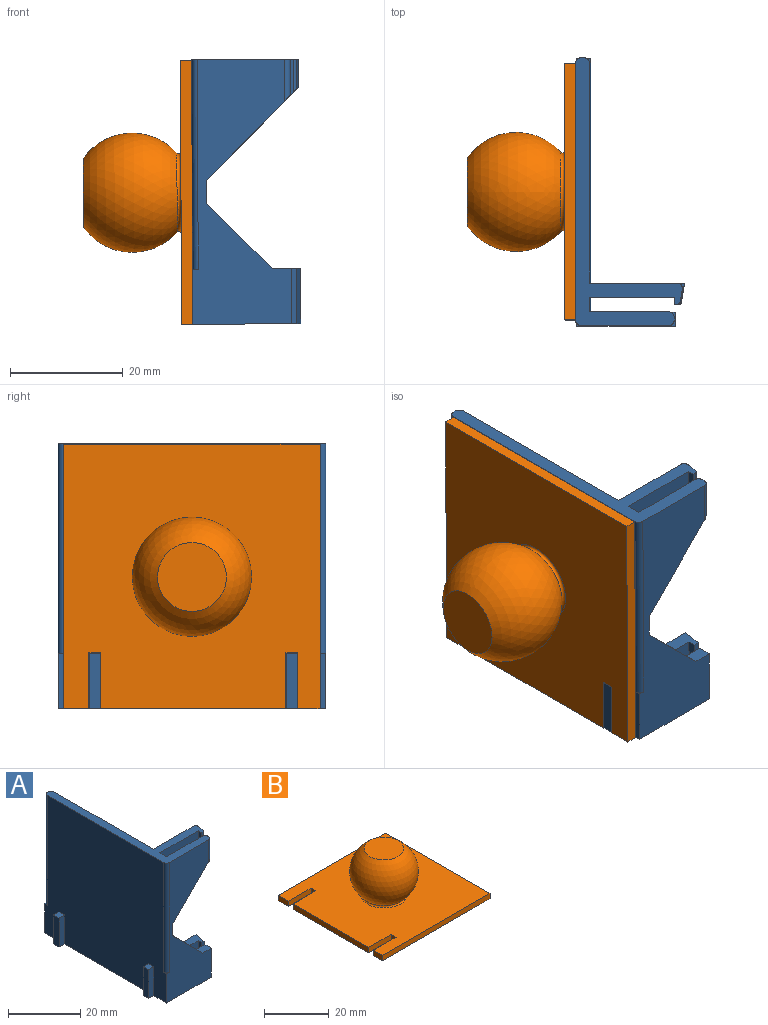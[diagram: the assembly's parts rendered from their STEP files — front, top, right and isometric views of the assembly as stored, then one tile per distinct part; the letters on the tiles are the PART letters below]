
ASSEMBLY  parts=2 mates=1
PART A: 44 faces, bbox 21.2x47.6x47 mm
  f0: plane 21.46x16.67mm, normal (0,1,0), area 231.3mm2, adj f5,f14,f19,f27,f32
  f1: plane 21.46x15mm, normal (0,1,0), area 215mm2, adj f7,f14,f19,f29,f31
  f2: plane 21.46x15mm, normal (0,-1,0), area 215mm2, adj f3,f14,f19,f27,f32
  f3: plane 9.8x1.3mm, normal (-1,0,0), area 12.7mm2, adj f2,f4,f19,f32
  f4: plane 9.8x1mm, normal (0,-1,0), area 9.8mm2, adj f3,f5,f19,f32
  f5: plane 9.8x3.79mm, normal (0.98,-0.17,0), area 37.7mm2, adj f0,f4,f19,f32
  f6: plane 47x17.49mm, normal (0,-1,0), area 497.3mm2, adj f7,f14,f16,f18,f19,f20,f24,f29
  f7: plane 9.8x2.49mm, normal (1,0,0), area 24.4mm2, adj f1,f6,f19,f31
  f8: plane 21.46x14mm, normal (0,1,0), area 202.5mm2, adj f14,f18,f21,f30
  f9: plane 21.46x15mm, normal (0,-1,0), area 209.4mm2, adj f10,f14,f18,f28
  f10: plane 6.46x1.3mm, normal (-1,0,0), area 8.4mm2, adj f9,f11,f18,f28
  f11: plane 6.46x0.58mm, normal (0,-1,0), area 3.6mm2, adj f10,f18,f26,f28
  f12: plane 5.39x2.2mm, normal (0.98,-0.17,0), area 11.6mm2, adj f18,f25,f26,f28
  f13: plane 21.46x15.48mm, normal (0,1,0), area 212.4mm2, adj f14,f18,f25,f28
  f14: plane 47.58x47mm, normal (1,0,0), area 1985.3mm2, adj f0,f1,f2,f6,f8,f9,f13,f15
  f15: plane 47x2.49mm, normal (0,1,0), area 42.6mm2, adj f14,f16,f18,f19,f22,f23,f34,f35
  f16: plane 47.58x47mm, normal (-1,0,0), area 2122.7mm2, adj f6,f15,f18,f19,f23,f24,f33,f34
  f17: plane 6.46x0.49mm, normal (1,0,0), area 3.2mm2, adj f18,f20,f21,f30
  f18: plane 47.58x18.97mm, normal (0,0,1), area 196.8mm2, adj f6,f8,f9,f10,f11,f12,f13,f14
  f19: plane 47.58x21.16mm, normal (0,0,-1), area 206.2mm2, adj f0,f1,f2,f3,f4,f5,f6,f7
  f20: cylinder r=1mm len=7.46mm, axis (0,0,-1), area 10.7mm2, adj f6,f17,f18,f30
  f21: cylinder r=1mm len=7.46mm, axis (0,0,-1), area 10.7mm2, adj f8,f17,f18,f30
  f22: cylinder r=1mm len=37.2mm, axis (0,0,1), area 58.4mm2, adj f14,f15,f18,f35
  f23: cylinder r=1mm len=37.2mm, axis (0,0,-1), area 58.4mm2, adj f15,f16,f18,f34
  f24: cylinder r=1mm len=37.2mm, axis (0,0,1), area 58.4mm2, adj f6,f16,f18,f33
  f25: cylinder r=1mm len=5.99mm, axis (0,0,1), area 9.3mm2, adj f12,f13,f18,f28
  f26: cylinder r=0.5mm len=5.88mm, axis (0,0,-1), area 3.9mm2, adj f11,f12,f18,f28
  f27: plane 11.66x11.66mm, normal (0.71,0,0.71), area 41.1mm2, adj f0,f2,f14,f32
  f28: plane 16.48x16.48mm, normal (0.71,0,-0.71), area 59.5mm2, adj f9,f10,f11,f12,f13,f14,f25,f26
  f29: plane 11.66x11.66mm, normal (0.71,0,0.71), area 41.1mm2, adj f1,f6,f14,f31
  f30: plane 15x15mm, normal (0.71,0,-0.71), area 52.2mm2, adj f6,f8,f14,f17,f20,f21
  f31: plane 3.34x2.49mm, normal (0,0,1), area 8.3mm2, adj f1,f6,f7,f29
  f32: plane 5.01x3.79mm, normal (0,0,1), area 13.4mm2, adj f0,f2,f3,f4,f5,f27
  f33: plane 1x1mm, normal (0,0,1), area 0.2mm2, adj f6,f16,f24
  f34: plane 1x1mm, normal (0,0,1), area 0.2mm2, adj f15,f16,f23
  f35: plane 1x1mm, normal (0,0,1), area 0.2mm2, adj f14,f15,f22
  f36: plane 9.8x2mm, normal (-1,0,0), area 19.6mm2, adj f19,f37,f38,f39
  f37: plane 2x2mm, normal (0,0,1), area 4mm2, adj f16,f36,f38,f39
  f38: plane 9.8x2mm, normal (0,1,0), area 19.6mm2, adj f16,f19,f36,f37
  f39: plane 9.8x2mm, normal (0,-1,0), area 19.6mm2, adj f16,f19,f36,f37
  f40: plane 2x2mm, normal (0,0,1), area 4mm2, adj f16,f41,f42,f43
  f41: plane 9.8x2mm, normal (0,1,0), area 19.6mm2, adj f16,f19,f40,f42
  f42: plane 9.8x2mm, normal (-1,0,0), area 19.6mm2, adj f19,f40,f41,f43
  f43: plane 9.8x2mm, normal (0,-1,0), area 19.6mm2, adj f16,f19,f40,f42
PART B: 17 faces, bbox 47x45.5x19.3 mm
  f0: sphere r=10.6mm, area 1106.9mm2, adj f15,f16
  f1: plane 45.5x2mm, normal (1,0,0), area 91mm2, adj f2,f12,f13,f14
  f2: plane 47x2mm, normal (0,-1,0), area 94mm2, adj f1,f3,f13,f14
  f3: plane 3.95x2mm, normal (-1,0,0), area 7.9mm2, adj f2,f4,f13,f14
  f4: plane 10x2mm, normal (0,1,0), area 20mm2, adj f3,f5,f13,f14
  f5: plane 2.1x2mm, normal (-1,0,0), area 4.2mm2, adj f4,f6,f13,f14
  f6: plane 10x2mm, normal (0,-1,0), area 20mm2, adj f5,f7,f13,f14
  f7: plane 32.9x2mm, normal (-1,0,0), area 65.8mm2, adj f6,f8,f13,f14
  f8: plane 10x2mm, normal (0,1,0), area 20mm2, adj f7,f9,f13,f14
  f9: plane 2.1x2mm, normal (-1,0,0), area 4.2mm2, adj f8,f10,f13,f14
  f10: plane 10x2mm, normal (0,-1,0), area 20mm2, adj f9,f11,f13,f14
  f11: plane 4.45x2mm, normal (-1,0,0), area 8.9mm2, adj f10,f12,f13,f14
  f12: plane 47x2mm, normal (0,1,0), area 94mm2, adj f1,f11,f13,f14
  f13: plane 47x45.5mm, normal (0,0,-1), area 2096.5mm2, adj f1,f2,f3,f4,f5,f6,f7,f8
  f14: plane 47x45.5mm, normal (0,0,1), area 1930.7mm2, adj f1,f2,f3,f4,f5,f6,f7,f8
  f15: torus R=7.26mm, axis (0,0,-1), area 42.4mm2, adj f0,f14
  f16: plane 12.22x12.22mm, normal (0,0,1), area 117.4mm2, adj f0
PLACE A rot(axis=(0,-1,0),0.3deg) t=(-12.58,-1.07,-11.94)mm
PLACE B rot(axis=(0,-1,0),90.3deg) t=(-14.69,22.73,11.45)mm
MATE slider A.f39 <-> B.f8  axis (0,-1,0) through (-14.61,38.93,-7.05)mm
